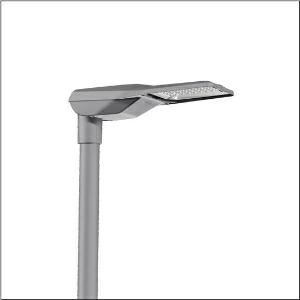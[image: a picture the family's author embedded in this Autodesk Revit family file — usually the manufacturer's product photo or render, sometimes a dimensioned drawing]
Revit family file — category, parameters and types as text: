
# Revit family: streetlight_sl_21_iq_mini___p1_0a_5xe2a41d08gb_135c
name_source: partatom
category: Lighting Fixtures
units: mm (PartAtom-declared; Revit-internal decimal feet)

## family parameters
Cut with Voids When Loaded = No
Host = Face
Light Source = No
Part Type = Normal
Room Calculation Point = No
Round Connector Dimension = Use Diameter
Shared = No

## types (1)
- --- (1 x LED, 5920 lm, 37.1 W, 4000K)
    Apparent Load = 37 VA
    CIE Flux Codes = 21 50 90 100 100
    Color Rendering = 70
    Color Temperature = 4000K
    Default Elevation = 1800 mm
    Description = Streetlight SL 21 iQ mini, mast luminaire, primary light control with lens, of PMMA, primary optical cover: cover, of toughened safety glass, transparent, light distribution: P1.0a, light emission: direct distribution, primary light characteristic: asymmetric, installation type: post-top, side-entry, LED, High Power LED, rated luminous flux: 5.920lm, luminous efficacy: 160lm/W, light colour: 740, colour temperature: 4000K, control: Auto-Match, Temp-Guard, Lumen-Switch, Night-Set, Smart-Wire, Light-Fading, Desk-Remote (wireless, voltage-free reading and setting of iQ features in the workshop via application-optimized NFC function/RFID function), optimised constant luminous flux control (CLO 2.0), presetting dimming linear, mains connection: 220..240V, AC, 50/60Hz, start of lifetime: 37W, end of service life: 39W, reduction: 18W, luminaire housing, of diecast aluminium, powder-coated, Siteco® metallic grey (DB 702S), corrosivity category C5 mid according to DIN EN ISO 12944, please order mast flange separately, inclination adjustable: 0°, 5°, 10°, 15°, sealing non-destructively replaceable, multi-level sealing system, length: 628mm, width: 235mm, height: 110mm, mast flange for spigot size: 42mm (side-entry): 5XC10008XM4, 60/48mm (side-entry/post-top): 5XC10108XM2, 76/60mm (side-entry/post-top): 5XC10108XM1, protection rating (complete): IP66, insulation class (complete): insulation class II (safety insulation), certification: CE, ENEC, ENEC+, VDE, impact resistance: IK09, permissible operating ambient temperature for outdoor applications: -40..+50°C, standard-compliant lighting for roads and squares, packaging unit: 1 piece

Light Distribution: P1.0a
    Height = 110 mm
    Lamp = 1 x LED
    Lamp Light Flux = 5920 lm
    Lamp Power = 37.1 W
    Lamp count = 1
    Length = 625 mm
    Luminous efficacy = 160 lm/W
    Manufacturer = Siteco
    ModVariant = No
    Model = 5XE2A41D08GB
    Number of Poles = 1
    OnlyDefault = Yes
    Power Factor = 1
    Product Name = Streetlight SL 21 iQ mini | P1.0a
    Product group = mast luminaire | pylon top
    ProductGroupID = 6100
    Protection Class = Protection class II
    Protection Degree = IP 66
    RLX_Detail_Level = 1
    RLX_Emergency_Light_Flux = 0 lm
    RLX_Emergency_Type = 0
    RLX_Emergency_Type_DB = No
    RlxData = <blob elided: 103569 chars, md5=c4f2315d>
    Socket = socket
    Standby Power = 0 W
    System Light Flux = 5920 lm
    System Power = 37 W
    Type Comments = factory setting: luminous flux: 100 % | dim-lin: 254 | 385 mA
    Type Image = l_1003519.jpg
    URL = http://relux.com
    VarID = @adj_120275
    Voltage = 0 V
    Weight = 0.00 kg
    Width = 234 mm

## geometry (parser evidence)
native form markers: Blend x4, Sweep x10
no freeform markers — native parametric forms only
